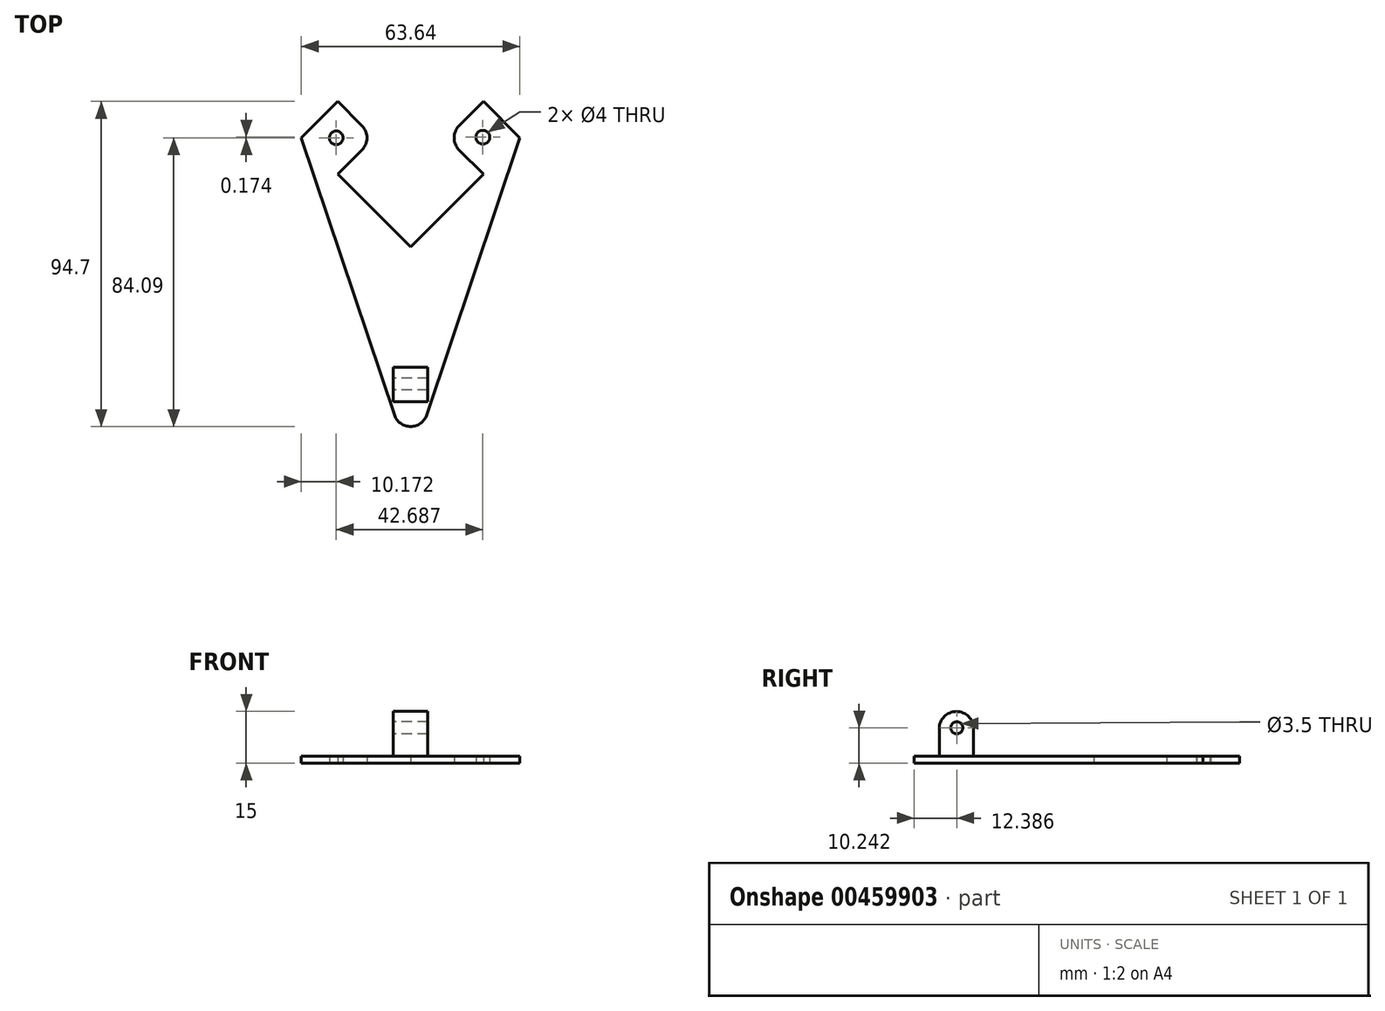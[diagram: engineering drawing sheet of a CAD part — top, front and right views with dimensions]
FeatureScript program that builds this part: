
annotation { "Feature Type Name" : "Feature", "Feature Type Description" : "" }
export const myFeature = defineFeature(function(context is Context, id is Id, definition is map)
    precondition{}
    {
        {
            var Q0;
            Q0=qCreatedBy(makeId("Top.planeOp"),FACE);
            var sketch = newSketch(context, id + "F0", { "sketchPlane" : qUnion([Q0])});
            skLineSegment(sketch, "E0", {"start": v(-30, 0) * mm, "end": v(0, 0) * mm});
            skLineSegment(sketch, "E1", {"start": v(0, 0) * mm, "end": v(0, 30) * mm});
            skLineSegment(sketch, "E2", {"start": v(0, 30) * mm, "end": v(-15, 30) * mm});
            skLineSegment(sketch, "E3", {"start": v(-15, 30) * mm, "end": v(-15, 45) * mm});
            skLineSegment(sketch, "E4", {"start": v(-15, 45) * mm, "end": v(0, 45) * mm});
            skLineSegment(sketch, "E5", {"start": v(0, 45) * mm, "end": v(44.54, -44.54) * mm});
            skLineSegment(sketch, "E6", {"start": v(44.54, -44.54) * mm, "end": v(-45, 0) * mm});
            skLineSegment(sketch, "E7", {"start": v(-45, 0) * mm, "end": v(-45, 15) * mm});
            skLineSegment(sketch, "E8", {"start": v(-45, 15) * mm, "end": v(-30, 15) * mm});
            skLineSegment(sketch, "E9", {"start": v(-30, 15) * mm, "end": v(-30, 0) * mm});
            skCircle(sketch, "E10", {"center": v(-7.75, 37.5) * mm, "radius": 2 * mm});
            skPoint(sketch, "E10.centerSnap0", {"position": v(-15, 37.5) * mm});
            skCircle(sketch, "E11", {"center": v(-37.8, 7.2) * mm, "radius": 2 * mm});
            skSolve(sketch);
        }
        {
            var Q0;
            Q0=makeQuery(id+"F0.imprint","IMPRINT",FACE,{"disambiguationData":[TD([[makeQuery(id+"F0.imprint","IMPRINT",EDGE,{"derivedFrom":sQuery(id+"F0.wireOp",EDGE,"E0")}),-1.0]])]});
            extrude(context, id + "F1", {"entities" : qUnion([Q0]), "depth" : 2 * mm});
        }
        {
            var Q0;
            Q0=makeQuery(id+"F1.opExtrude","SWEPT_BODY",BODY,{"disambiguationData":[OSD([sQuery(id+"F0.wireOp",EDGE,"E0"),sQuery(id+"F0.wireOp",EDGE,"E1"),sQuery(id+"F0.wireOp",EDGE,"E2"),sQuery(id+"F0.wireOp",EDGE,"E3"),sQuery(id+"F0.wireOp",EDGE,"E4"),sQuery(id+"F0.wireOp",EDGE,"E5"),sQuery(id+"F0.wireOp",EDGE,"E6"),sQuery(id+"F0.wireOp",EDGE,"E7"),sQuery(id+"F0.wireOp",EDGE,"E8"),sQuery(id+"F0.wireOp",EDGE,"E9"),sQuery(id+"F0.wireOp",EDGE,"E10"),sQuery(id+"F0.wireOp",EDGE,"E11")])]});
            var Q1;
            Q1=makeQuery(id+"F1.opExtrude","SWEPT_EDGE",EDGE,{"disambiguationData":[OSD([sQuery(id+"F0.wireOp",EDGE,"E0"),sQuery(id+"F0.wireOp",EDGE,"E1")])]});
            transform(context, id + "F2", {"entities" : qUnion([Q0]), "transformType" : TransformType.ROTATION, "transformAxis" : qUnion([Q1]), "angle" : 45 * degree, "makeCopy" : false});
        }
        {
            var Q0;
            Q0=qCreatedBy(makeId("Right.planeOp"),FACE);
            var sketch = newSketch(context, id + "F3", { "sketchPlane" : qUnion([Q0])});
            skLineSegment(sketch, "E12.bottom", {"start": v(-35, 0) * mm, "end": v(-45, 0) * mm});
            skLineSegment(sketch, "E12.top", {"start": v(-35, 15) * mm, "end": v(-45, 15) * mm});
            skLineSegment(sketch, "E12.left", {"start": v(-35, 0) * mm, "end": v(-35, 15) * mm});
            skLineSegment(sketch, "E12.right", {"start": v(-45, 0) * mm, "end": v(-45, 15) * mm});
            skCircle(sketch, "E13", {"center": v(-39.88, 10.24) * mm, "radius": 1.75 * mm});
            skLineSegment(sketch, "E14", {"start": v(0, 0) * mm, "end": v(-35, 0) * mm});
            skSolve(sketch);
        }
        {
            var Q0;
            Q0=makeQuery(id+"F3.imprint","IMPRINT",FACE,{"disambiguationData":[TD([[makeQuery(id+"F3.imprint","IMPRINT",EDGE,{"derivedFrom":sQuery(id+"F3.wireOp",EDGE,"E12.bottom")}),-1.0]])]});
            extrude(context, id + "F4", {"entities" : qUnion([Q0]), "operationType" : NewBodyOperationType.ADD, "endBound" : BoundingType.SYMMETRIC, "depth" : 10 * mm});
        }
        {
            var Q0;
            Q0=makeQuery(id+"F4.opExtrude","SWEPT_EDGE",EDGE,{"disambiguationData":[OSD([sQuery(id+"F3.wireOp",EDGE,"E12.top"),sQuery(id+"F3.wireOp",EDGE,"E12.right")])]});
            var Q1;
            Q1=makeQuery(id+"F4.opExtrude","SWEPT_EDGE",EDGE,{"disambiguationData":[OSD([sQuery(id+"F3.wireOp",EDGE,"E12.top"),sQuery(id+"F3.wireOp",EDGE,"E12.left")])]});
            var Q2;
            Q2=makeQuery(id+"F1.opExtrude","SWEPT_EDGE",EDGE,{"disambiguationData":[OSD([sQuery(id+"F0.wireOp",EDGE,"E2"),sQuery(id+"F0.wireOp",EDGE,"E3")])]});
            var Q3;
            Q3=makeQuery(id+"F1.opExtrude","SWEPT_EDGE",EDGE,{"disambiguationData":[OSD([sQuery(id+"F0.wireOp",EDGE,"E8"),sQuery(id+"F0.wireOp",EDGE,"E9")])]});
            fillet(context, id + "F5", {"entities" : qUnion([Q0, Q1, Q2, Q3]), "radius" : 5 * mm, "tangentPropagation" : true, "allowEdgeOverflow" : false});
        }
        {
            var Q0;
            Q0=makeQuery(id+"F1.opExtrude","SWEPT_EDGE",EDGE,{"disambiguationData":[OSD([sQuery(id+"F0.wireOp",EDGE,"E5"),sQuery(id+"F0.wireOp",EDGE,"E6")])]});
            fillet(context, id + "F6", {"entities" : qUnion([Q0]), "radius" : 5 * mm, "tangentPropagation" : true, "allowEdgeOverflow" : false});
        }
    });
